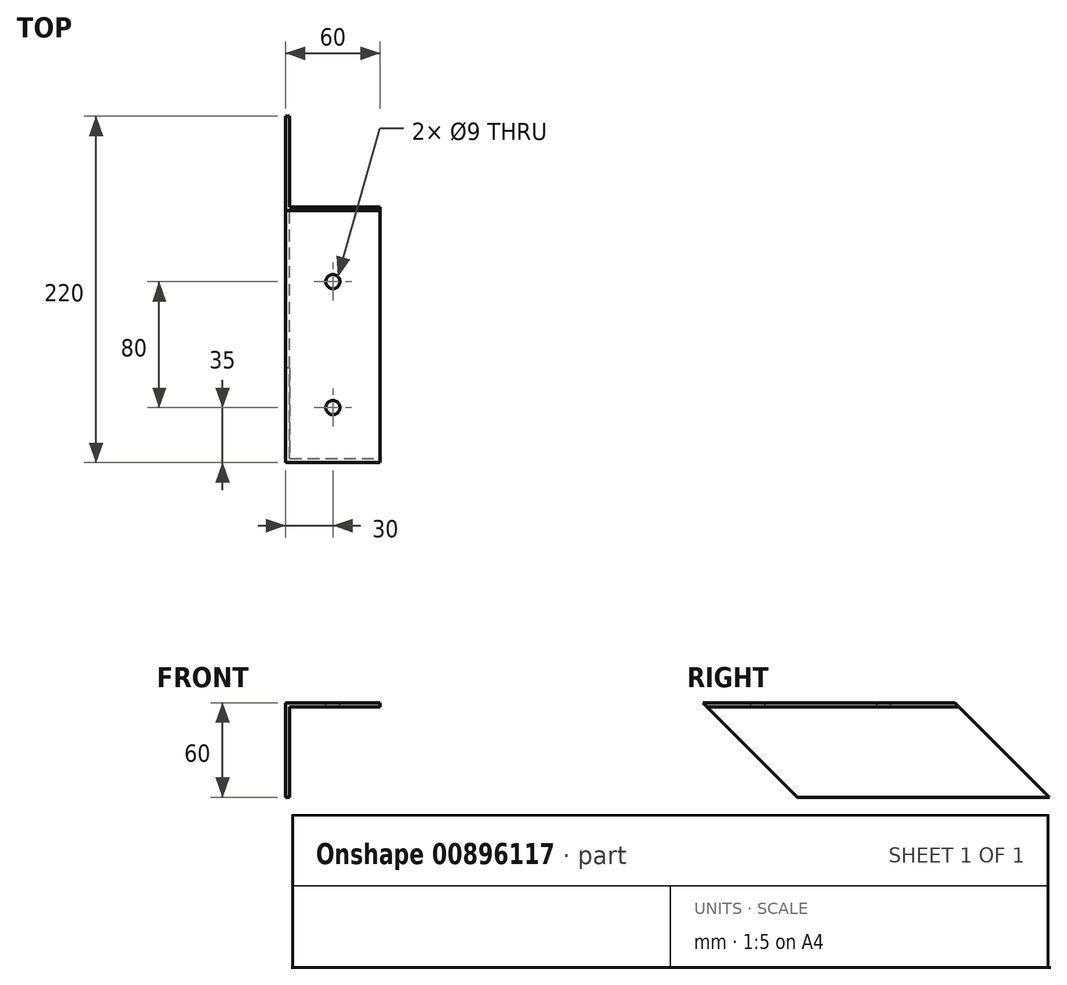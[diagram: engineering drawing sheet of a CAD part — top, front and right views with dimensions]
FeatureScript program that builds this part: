
annotation { "Feature Type Name" : "Feature", "Feature Type Description" : "" }
export const myFeature = defineFeature(function(context is Context, id is Id, definition is map)
    precondition{}
    {
        {
            var Q0;
            Q0=qCreatedBy(makeId("Front.planeOp"),FACE);
            var sketch = newSketch(context, id + "F0", { "sketchPlane" : qUnion([Q0])});
            skLineSegment(sketch, "E0", {"start": v(0, 0) * mm, "end": v(60, 0) * mm});
            skLineSegment(sketch, "E1", {"start": v(60, 0) * mm, "end": v(60, -2.5) * mm});
            skLineSegment(sketch, "E2", {"start": v(60, -2.5) * mm, "end": v(2.5, -2.5) * mm});
            skLineSegment(sketch, "E3", {"start": v(2.5, -2.5) * mm, "end": v(2.5, -60) * mm});
            skLineSegment(sketch, "E4", {"start": v(2.5, -60) * mm, "end": v(0, -60) * mm});
            skLineSegment(sketch, "E5", {"start": v(0, -60) * mm, "end": v(0, 0) * mm});
            skSolve(sketch);
        }
        {
            var Q0;
            Q0=qSketchRegion(id+"F0",true);
            extrude(context, id + "F1", {"entities" : qUnion([Q0]), "depth" : 220 * mm, "offsetDistance" : 25 * mm});
        }
        {
            var Q0;
            Q0=makeQuery(id+"F1.opExtrude","SWEPT_FACE",FACE,{"disambiguationData":[OSD([sQuery(id+"F0.wireOp",EDGE,"E5")])]});
            var sketch = newSketch(context, id + "F2", { "sketchPlane" : qUnion([Q0])});
            skLineSegment(sketch, "E6", {"start": v(0, -60) * mm, "end": v(60, 0) * mm});
            skLineSegment(sketch, "E7", {"start": v(60, 0) * mm, "end": v(0, 0) * mm});
            skLineSegment(sketch, "E8", {"start": v(0, 0) * mm, "end": v(0, -60) * mm});
            skLineSegment(sketch, "E9", {"start": v(220, 0) * mm, "end": v(160, -60) * mm});
            skLineSegment(sketch, "E10", {"start": v(160, -60) * mm, "end": v(220, -60) * mm});
            skLineSegment(sketch, "E11", {"start": v(220, -60) * mm, "end": v(220, 0) * mm});
            skSolve(sketch);
        }
        {
            var Q0;
            Q0=qSketchRegion(id+"F2",true);
            extrude(context, id + "F3", {"entities" : qUnion([Q0]), "operationType" : NewBodyOperationType.REMOVE, "endBound" : BoundingType.THROUGH_ALL, "oppositeDirection" : true, "depth" : 25 * mm, "offsetDistance" : 25 * mm});
        }
        {
            var Q0;
            Q0=makeQuery(id+"F1.opExtrude","SWEPT_FACE",FACE,{"disambiguationData":[OSD([sQuery(id+"F0.wireOp",EDGE,"E0")])]});
            var sketch = newSketch(context, id + "F4", { "sketchPlane" : qUnion([Q0])});
            skLineSegment(sketch, "E12", {"start": v(30, -60) * mm, "end": v(30, -105) * mm, "construction": true});
            skLineSegment(sketch, "E13", {"start": v(30, -105) * mm, "end": v(30, -185) * mm, "construction": true});
            skLineSegment(sketch, "E14", {"start": v(30, -185) * mm, "end": v(30, -220) * mm, "construction": true});
            skCircle(sketch, "E15", {"center": v(30, -105) * mm, "radius": 4.5 * mm});
            skCircle(sketch, "E16", {"center": v(30, -185) * mm, "radius": 4.5 * mm});
            skSolve(sketch);
        }
        {
            var Q0;
            Q0=qSketchRegion(id+"F4",true);
            extrude(context, id + "F5", {"entities" : qUnion([Q0]), "operationType" : NewBodyOperationType.REMOVE, "endBound" : BoundingType.THROUGH_ALL, "oppositeDirection" : true, "depth" : 25 * mm, "offsetDistance" : 25 * mm});
        }
    });
